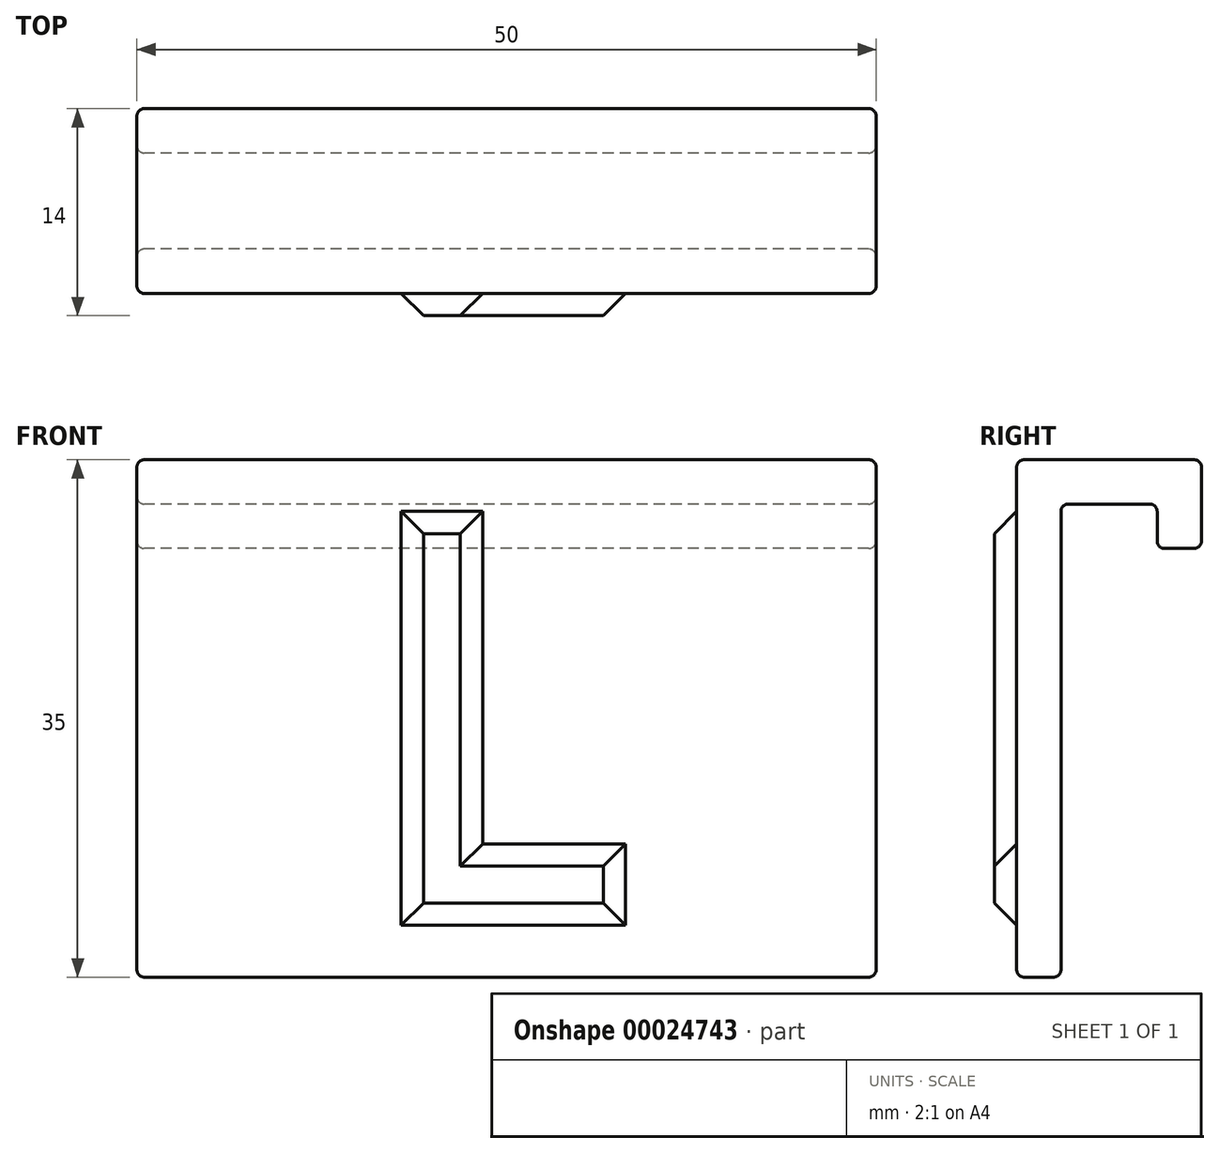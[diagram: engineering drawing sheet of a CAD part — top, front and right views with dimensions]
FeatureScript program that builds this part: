
annotation { "Feature Type Name" : "Feature", "Feature Type Description" : "" }
export const myFeature = defineFeature(function(context is Context, id is Id, definition is map)
    precondition{}
    {
        {
            var Q0;
            Q0=qCreatedBy(makeId("Right.planeOp"),FACE);
            var sketch = newSketch(context, id + "F0", { "sketchPlane" : qUnion([Q0])});
            skLineSegment(sketch, "E0", {"start": v(0, 0) * mm, "end": v(0, 35) * mm});
            skLineSegment(sketch, "E1", {"start": v(0, 35) * mm, "end": v(12.5, 35) * mm});
            skLineSegment(sketch, "E2", {"start": v(12.5, 35) * mm, "end": v(12.5, 29) * mm});
            skLineSegment(sketch, "E3", {"start": v(12.5, 29) * mm, "end": v(9.5, 29) * mm});
            skLineSegment(sketch, "E4", {"start": v(9.5, 29) * mm, "end": v(9.5, 32) * mm});
            skLineSegment(sketch, "E5", {"start": v(9.5, 32) * mm, "end": v(3, 32) * mm});
            skLineSegment(sketch, "E6", {"start": v(3, 32) * mm, "end": v(3, 0) * mm});
            skLineSegment(sketch, "E7", {"start": v(3, 0) * mm, "end": v(0, 0) * mm});
            skSolve(sketch);
        }
        {
            var Q0;
            Q0 = qSketchRegion(id + "F0", true);
            extrude(context, id + "F1", {"entities" : qUnion([Q0]), "depth" : 50 * mm});
        }
        {
            var Q0;
            Q0=makeQuery(id+"F1.opExtrude","SWEPT_FACE",FACE,{"disambiguationData":[OSD([sQuery(id+"F0.wireOp",EDGE,"E0")])]});
            var sketch = newSketch(context, id + "F2", { "sketchPlane" : qUnion([Q0])});
            skLineSegment(sketch, "E8", {"start": v(17.5, 35) * mm, "end": v(17.5, 0) * mm});
            skLineSegment(sketch, "E9", {"start": v(33.42, 35) * mm, "end": v(33.42, 0) * mm});
            skLineSegment(sketch, "E10", {"start": v(0, 5) * mm, "end": v(50, 5) * mm});
            skLineSegment(sketch, "E11", {"start": v(2.5, 35) * mm, "end": v(2.5, 0) * mm});
            skLineSegment(sketch, "E12", {"start": v(47.5, 35) * mm, "end": v(47.5, 0) * mm});
            skLineSegment(sketch, "E13", {"start": v(5, 30) * mm, "end": v(6.86, 30) * mm});
            skLineSegment(sketch, "E14", {"start": v(7.5, 5) * mm, "end": v(5, 5) * mm});
            skPoint(sketch, "E15", {"position": v(2.5, 30) * mm});
            skPoint(sketch, "E16", {"position": v(17.5, 30) * mm});
            skPoint(sketch, "E17", {"position": v(33.42, 30.72) * mm});
            skPoint(sketch, "E18", {"position": v(47.5, 30) * mm});
            skPoint(sketch, "E19", {"position": v(47.5, 5) * mm});
            skPoint(sketch, "E20", {"position": v(33.42, 5) * mm});
            skPoint(sketch, "E21", {"position": v(17.5, 5) * mm});
            skPoint(sketch, "E22", {"position": v(2.5, 5) * mm});
            skLineSegment(sketch, "E23", {"start": v(2.5, 30) * mm, "end": v(5, 30) * mm});
            skLineSegment(sketch, "E24", {"start": v(5, 30) * mm, "end": v(5, 5) * mm});
            skLineSegment(sketch, "E25", {"start": v(17.5, 30) * mm, "end": v(16.25, 30) * mm});
            skLineSegment(sketch, "E26", {"start": v(16.25, 30) * mm, "end": v(16.25, 27.5) * mm});
            skPoint(sketch, "E27", {"position": v(5, 17.5) * mm});
            skLineSegment(sketch, "E28", {"start": v(5, 17.5) * mm, "end": v(5, 20) * mm});
            skLineSegment(sketch, "E29", {"start": v(16.25, 27.5) * mm, "end": v(16.25, 20) * mm});
            skLineSegment(sketch, "E30", {"start": v(7.5, 5) * mm, "end": v(7.5, 17.5) * mm});
            skLineSegment(sketch, "E31", {"start": v(7.5, 20) * mm, "end": v(7.5, 27.5) * mm});
            skLineSegment(sketch, "E32", {"start": v(16.25, 30) * mm, "end": v(13.75, 30) * mm});
            skLineSegment(sketch, "E33", {"start": v(5, 30) * mm, "end": v(13.75, 30) * mm});
            skLineSegment(sketch, "E34", {"start": v(13.75, 30) * mm, "end": v(16.25, 27.5) * mm});
            skLineSegment(sketch, "E35", {"start": v(13.75, 26.46) * mm, "end": v(13.75, 21.04) * mm});
            skLineSegment(sketch, "E36", {"start": v(7.5, 17.5) * mm, "end": v(13.75, 17.5) * mm});
            skLineSegment(sketch, "E37", {"start": v(13.75, 17.5) * mm, "end": v(16.25, 20) * mm});
            skPoint(sketch, "E38.trimOffspring.end.orphan", {"position": v(0, 30) * mm});
            skPoint(sketch, "E39.orphan", {"position": v(13.75, 20) * mm});
            skPoint(sketch, "E40.orphan", {"position": v(15, 18.75) * mm});
            skPoint(sketch, "E41.orphan", {"position": v(13.75, 27.5) * mm});
            skPoint(sketch, "E42.start.orphan", {"position": v(15, 28.75) * mm});
            skLineSegment(sketch, "E43", {"start": v(17.5, 30) * mm, "end": v(19.38, 30) * mm});
            skLineSegment(sketch, "E44", {"start": v(19.38, 30) * mm, "end": v(19.38, 5) * mm});
            skLineSegment(sketch, "E45", {"start": v(19.38, 5) * mm, "end": v(31.55, 5) * mm});
            skLineSegment(sketch, "E46", {"start": v(31.55, 5) * mm, "end": v(33.42, 5) * mm});
            skLineSegment(sketch, "E47", {"start": v(31.55, 5) * mm, "end": v(31.55, 7.5) * mm});
            skLineSegment(sketch, "E48", {"start": v(31.55, 7.5) * mm, "end": v(21.88, 7.5) * mm});
            skLineSegment(sketch, "E49", {"start": v(21.88, 7.5) * mm, "end": v(21.88, 30) * mm});
            skLineSegment(sketch, "E50", {"start": v(21.88, 30) * mm, "end": v(19.38, 30) * mm});
            skLineSegment(sketch, "E51", {"start": v(33.42, 5) * mm, "end": v(34.67, 5) * mm});
            skLineSegment(sketch, "E52", {"start": v(34.67, 5) * mm, "end": v(37.17, 5) * mm});
            skLineSegment(sketch, "E53", {"start": v(47.5, 5) * mm, "end": v(45, 5) * mm});
            skLineSegment(sketch, "E54", {"start": v(45, 5) * mm, "end": v(42.5, 5) * mm});
            skLineSegment(sketch, "E55", {"start": v(37.17, 5) * mm, "end": v(42.5, 5) * mm});
            skLineSegment(sketch, "E56", {"start": v(39.27, 30.72) * mm, "end": v(37.4, 30.72) * mm});
            skLineSegment(sketch, "E57", {"start": v(39.27, 30.72) * mm, "end": v(41.14, 30.72) * mm});
            skLineSegment(sketch, "E58", {"start": v(37.4, 30.72) * mm, "end": v(34.67, 5) * mm});
            skLineSegment(sketch, "E59", {"start": v(41.14, 30.72) * mm, "end": v(45, 5) * mm});
            skLineSegment(sketch, "E60", {"start": v(37.17, 5) * mm, "end": v(38.23, 15) * mm});
            skLineSegment(sketch, "E61", {"start": v(42.5, 5) * mm, "end": v(41, 15) * mm});
            skLineSegment(sketch, "E62", {"start": v(38.5, 17.5) * mm, "end": v(40.62, 17.5) * mm});
            skLineSegment(sketch, "E63.trimOffspring", {"start": v(38.5, 17.5) * mm, "end": v(39.38, 25.83) * mm});
            skLineSegment(sketch, "E64.trimOffspring", {"start": v(40.62, 17.5) * mm, "end": v(39.38, 25.83) * mm});
            skPoint(sketch, "E65.orphan", {"position": v(39.84, 5) * mm});
            skLineSegment(sketch, "E66", {"start": v(39.6, 15) * mm, "end": v(38.23, 15) * mm});
            skLineSegment(sketch, "E67", {"start": v(39.6, 15) * mm, "end": v(41, 15) * mm});
            skPoint(sketch, "E68.orphan", {"position": v(38.27, 15.42) * mm});
            skPoint(sketch, "E69.orphan", {"position": v(40.94, 15.42) * mm});
            skPoint(sketch, "E70.start.orphan", {"position": v(39.56, 17.5) * mm});
            skLineSegment(sketch, "E71", {"start": v(13.23, 26.98) * mm, "end": v(13.75, 26.46) * mm});
            skLineSegment(sketch, "E72", {"start": v(13.23, 26.98) * mm, "end": v(12.71, 27.5) * mm});
            skLineSegment(sketch, "E73", {"start": v(12.71, 27.5) * mm, "end": v(7.5, 27.5) * mm});
            skLineSegment(sketch, "E74", {"start": v(13.75, 21.04) * mm, "end": v(12.71, 20) * mm});
            skLineSegment(sketch, "E75", {"start": v(7.5, 20) * mm, "end": v(12.71, 20) * mm});
            skSolve(sketch);
        }
        {
            var Q0;
            {var subQ6=sQuery(id+"F2.wireOp",EDGE,"E14");Q0=makeQuery(id+"F2.imprint","IMPRINT",FACE,{"disambiguationData":[TD([[makeQuery(id+"F2.imprint","IMPRINT",EDGE,{"derivedFrom":subQ6}),-1.0]])]});}
            var Q1;
            Q1=makeQuery(id+"F2.imprint","IMPRINT",FACE,{"disambiguationData":[TD([[makeQuery(id+"F2.imprint","IMPRINT",EDGE,{"derivedFrom":sQuery(id+"F2.wireOp",EDGE,"E44")}),1.0]])]});
            var Q2;
            Q2=makeQuery(id+"F2.imprint","IMPRINT",FACE,{"disambiguationData":[TD([[makeQuery(id+"F2.imprint","IMPRINT",EDGE,{"derivedFrom":sQuery(id+"F2.wireOp",EDGE,"E52")}),1.0]])]});
            extrude(context, id + "F3", {"entities" : qUnion([Q0, Q1, Q2]), "operationType" : NewBodyOperationType.ADD, "depth" : 1.5 * mm});
        }
        {
            var Q0;
            Q0=makeQuery(id+"F1.opExtrude","SWEPT_FACE",FACE,{"disambiguationData":[OSD([sQuery(id+"F0.wireOp",EDGE,"E1")])]});
            var Q1;
            Q1=makeQuery(id+"F1.opExtrude","CAP_FACE",FACE,{"disambiguationData":[OSD([sQuery(id+"F0.wireOp",EDGE,"E0"),sQuery(id+"F0.wireOp",EDGE,"E1"),sQuery(id+"F0.wireOp",EDGE,"E2"),sQuery(id+"F0.wireOp",EDGE,"E3"),sQuery(id+"F0.wireOp",EDGE,"E4"),sQuery(id+"F0.wireOp",EDGE,"E5"),sQuery(id+"F0.wireOp",EDGE,"E6"),sQuery(id+"F0.wireOp",EDGE,"E7")])],"isStart":false});
            var Q2;
            Q2=makeQuery(id+"F1.opExtrude","CAP_FACE",FACE,{"disambiguationData":[OSD([sQuery(id+"F0.wireOp",EDGE,"E0"),sQuery(id+"F0.wireOp",EDGE,"E1"),sQuery(id+"F0.wireOp",EDGE,"E2"),sQuery(id+"F0.wireOp",EDGE,"E3"),sQuery(id+"F0.wireOp",EDGE,"E4"),sQuery(id+"F0.wireOp",EDGE,"E5"),sQuery(id+"F0.wireOp",EDGE,"E6"),sQuery(id+"F0.wireOp",EDGE,"E7")])],"isStart":true});
            var Q3;
            Q3=makeQuery(id+"F1.opExtrude","SWEPT_FACE",FACE,{"disambiguationData":[OSD([sQuery(id+"F0.wireOp",EDGE,"E2")])]});
            var Q4;
            Q4=makeQuery(id+"F1.opExtrude","SWEPT_FACE",FACE,{"disambiguationData":[OSD([sQuery(id+"F0.wireOp",EDGE,"E3")])]});
            var Q5;
            Q5=makeQuery(id+"F1.opExtrude","SWEPT_FACE",FACE,{"disambiguationData":[OSD([sQuery(id+"F0.wireOp",EDGE,"E5")])]});
            var Q6;
            Q6=makeQuery(id+"F1.opExtrude","SWEPT_FACE",FACE,{"disambiguationData":[OSD([sQuery(id+"F0.wireOp",EDGE,"E6")])]});
            var Q7;
            Q7=makeQuery(id+"F1.opExtrude","SWEPT_FACE",FACE,{"disambiguationData":[OSD([sQuery(id+"F0.wireOp",EDGE,"E7")])]});
            fillet(context, id + "F4", {"entities" : qUnion([Q0, Q1, Q2, Q3, Q4, Q5, Q6, Q7]), "radius" : .5 * mm, "tangentPropagation" : true, "allowEdgeOverflow" : false});
        }
        {
            var Q0;
            {var subQ0=sQuery(id+"F0.wireOp",EDGE,"E0");var subQ1=sQuery(id+"F0.wireOp",EDGE,"E1");Q0=makeQuery(id+"F3.boolean.opBoolean","SPLIT",FACE,{"disambiguationData":[TD([makeQuery(id+"F1.opExtrude","SWEPT_FACE",FACE,{"disambiguationData":[OSD([subQ1])]})])],"derivedFrom":makeQuery(id+"F1.opExtrude","SWEPT_FACE",FACE,{"disambiguationData":[OSD([subQ0])]})});}
            var Q1;
            Q1=makeQuery(id+"F3.boolean.opBoolean","SPLIT",FACE,{"disambiguationData":[TD([makeQuery(id+"F3.opExtrude","SWEPT_FACE",FACE,{"disambiguationData":[OSD([sQuery(id+"F2.wireOp",EDGE,"E31")])]})])],"derivedFrom":makeQuery(id+"F1.opExtrude","SWEPT_FACE",FACE,{"disambiguationData":[OSD([sQuery(id+"F0.wireOp",EDGE,"E0")])]})});
            var Q2;
            Q2=makeQuery(id+"F3.opExtrude","CAP_EDGE",EDGE,{"disambiguationData":[OSD([sQuery(id+"F2.wireOp",EDGE,"E62")])],"isStart":true});
            chamfer(context, id + "F5", {"entities" : qUnion([Q0, Q1, Q2]), "width" : 1.5 * mm, "tangentPropagation" : true});
        }
    });
